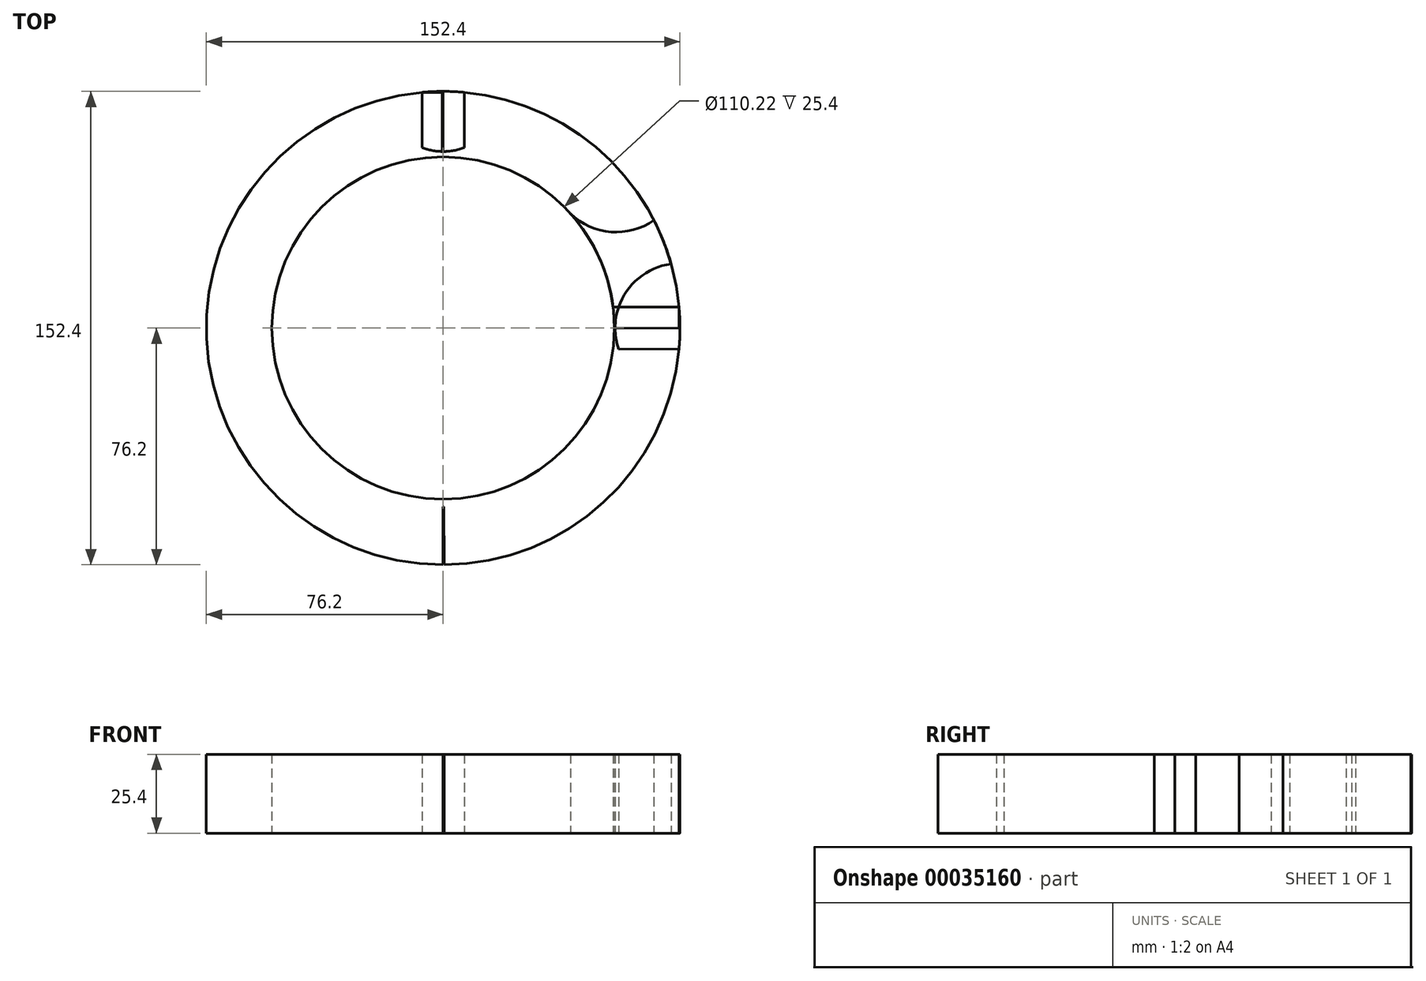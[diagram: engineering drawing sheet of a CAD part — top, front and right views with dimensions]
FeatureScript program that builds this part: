
annotation { "Feature Type Name" : "Feature", "Feature Type Description" : "" }
export const myFeature = defineFeature(function(context is Context, id is Id, definition is map)
    precondition{}
    {
        {
            var Q0;
            Q0=qCreatedBy(makeId("Top.planeOp"),FACE);
            var sketch = newSketch(context, id + "F0", { "sketchPlane" : qUnion([Q0])});
            skCircle(sketch, "E0", {"center": v(0, 0) * mm, "radius": 76.2 * mm});
            skLineSegment(sketch, "E1.bottom", {"start": v(-6.77, 75.9) * mm, "end": v(0, 75.9) * mm});
            skLineSegment(sketch, "E1.top", {"start": v(-6.77, -76.2) * mm, "end": v(0, -76.2) * mm});
            skLineSegment(sketch, "E1.left", {"start": v(-6.77, 75.9) * mm, "end": v(-6.77, -76.2) * mm});
            skLineSegment(sketch, "E1.right", {"start": v(0, 75.9) * mm, "end": v(0, -76.2) * mm});
            skLineSegment(sketch, "E2.MirrorCS", {"start": v(6.77, 75.9) * mm, "end": v(6.77, -76.2) * mm});
            skLineSegment(sketch, "E3", {"start": v(75.9, 6.7) * mm, "end": v(0, 6.7) * mm});
            skLineSegment(sketch, "E4", {"start": v(75.9, 0) * mm, "end": v(0, -0.15) * mm});
            skLineSegment(sketch, "E5.MirrorCS", {"start": v(75.93, -6.7) * mm, "end": v(0.03, -7.01) * mm});
            skLineSegment(sketch, "E6.MirrorCS", {"start": v(0.3, -76.2) * mm, "end": v(-0.3, 75.9) * mm});
            skLineSegment(sketch, "E7.MirrorCS", {"start": v(-75.9, 6.7) * mm, "end": v(0, 6.7) * mm});
            skLineSegment(sketch, "E8.MirrorCS", {"start": v(-75.93, -6.7) * mm, "end": v(-0.03, -7.01) * mm});
            skLineSegment(sketch, "E9", {"start": v(-76.2, 0) * mm, "end": v(-0.03, -0.3) * mm});
            skCircle(sketch, "E10", {"center": v(0, 75.9) * mm, "radius": 19.05 * mm});
            skCircle(sketch, "E11", {"center": v(-55.68, 52.02) * mm, "radius": 21.13 * mm});
            skCircle(sketch, "E12.MirrorC", {"center": v(-56.1, -52.18) * mm, "radius": 21.13 * mm});
            skCircle(sketch, "E13.MirrorC", {"center": v(-0.6, -76.5) * mm, "radius": 19.05 * mm});
            skCircle(sketch, "E14.MirrorC", {"center": v(56.1, -52.18) * mm, "radius": 21.13 * mm});
            skCircle(sketch, "E15.MirrorC", {"center": v(55.68, 52.02) * mm, "radius": 21.13 * mm});
            skCircle(sketch, "E16", {"center": v(-76.2, 0) * mm, "radius": 20.86 * mm});
            skCircle(sketch, "E17.MirrorC", {"center": v(76.2, 0) * mm, "radius": 20.86 * mm});
            skCircle(sketch, "E18", {"center": v(0, 0) * mm, "radius": 55.1 * mm});
            skLineSegment(sketch, "E19.bottom", {"start": v(75.9, 0) * mm, "end": v(97.82, 0) * mm});
            skLineSegment(sketch, "E19.top", {"start": v(75.9, 21.09) * mm, "end": v(97.82, 21.09) * mm});
            skLineSegment(sketch, "E19.left", {"start": v(75.9, 0) * mm, "end": v(75.9, 21.09) * mm});
            skLineSegment(sketch, "E19.right", {"start": v(97.82, 0) * mm, "end": v(97.82, 21.09) * mm});
            skLineSegment(sketch, "E20.bottom", {"start": v(55.68, 52.02) * mm, "end": v(75.71, 52.02) * mm});
            skLineSegment(sketch, "E20.top", {"start": v(55.68, 73.25) * mm, "end": v(75.71, 73.25) * mm});
            skLineSegment(sketch, "E20.left", {"start": v(55.68, 52.02) * mm, "end": v(55.68, 73.25) * mm});
            skLineSegment(sketch, "E20.right", {"start": v(75.71, 52.02) * mm, "end": v(75.71, 73.25) * mm});
            skLineSegment(sketch, "E21.bottom", {"start": v(-0.3, 75.9) * mm, "end": v(-19.7, 75.9) * mm});
            skLineSegment(sketch, "E21.top", {"start": v(-0.3, 95.36) * mm, "end": v(-19.7, 95.36) * mm});
            skLineSegment(sketch, "E21.left", {"start": v(-0.3, 75.9) * mm, "end": v(-0.3, 95.36) * mm});
            skLineSegment(sketch, "E21.right", {"start": v(-19.7, 75.9) * mm, "end": v(-19.7, 95.36) * mm});
            skLineSegment(sketch, "E22.bottom", {"start": v(-55.68, 52.02) * mm, "end": v(-76.2, 52.02) * mm});
            skLineSegment(sketch, "E22.top", {"start": v(-55.68, 74.45) * mm, "end": v(-76.2, 74.45) * mm});
            skLineSegment(sketch, "E22.left", {"start": v(-55.68, 52.02) * mm, "end": v(-55.68, 74.45) * mm});
            skLineSegment(sketch, "E22.right", {"start": v(-76.2, 52.02) * mm, "end": v(-76.2, 74.45) * mm});
            skLineSegment(sketch, "E23.bottom", {"start": v(-76.2, 0) * mm, "end": v(-97.1, 0) * mm});
            skLineSegment(sketch, "E23.top", {"start": v(-76.2, 20.85) * mm, "end": v(-97.1, 20.85) * mm});
            skLineSegment(sketch, "E23.left", {"start": v(-76.2, 0) * mm, "end": v(-76.2, 20.85) * mm});
            skLineSegment(sketch, "E23.right", {"start": v(-97.1, 0) * mm, "end": v(-97.1, 20.85) * mm});
            skLineSegment(sketch, "E24.bottom", {"start": v(-56.1, -52.18) * mm, "end": v(-76.67, -52.18) * mm});
            skLineSegment(sketch, "E24.top", {"start": v(-56.1, -74.09) * mm, "end": v(-76.67, -74.09) * mm});
            skLineSegment(sketch, "E24.left", {"start": v(-56.1, -52.18) * mm, "end": v(-56.1, -74.09) * mm});
            skLineSegment(sketch, "E24.right", {"start": v(-76.67, -52.18) * mm, "end": v(-76.67, -74.09) * mm});
            skLineSegment(sketch, "E25.bottom", {"start": v(0.3, -76.5) * mm, "end": v(-19.23, -76.5) * mm});
            skLineSegment(sketch, "E25.top", {"start": v(0.3, -96.2) * mm, "end": v(-19.23, -96.2) * mm});
            skLineSegment(sketch, "E25.left", {"start": v(0.3, -76.5) * mm, "end": v(0.3, -96.2) * mm});
            skLineSegment(sketch, "E25.right", {"start": v(-19.23, -76.5) * mm, "end": v(-19.23, -96.2) * mm});
            skLineSegment(sketch, "E26.bottom", {"start": v(56.1, -52.18) * mm, "end": v(76.2, -52.18) * mm});
            skLineSegment(sketch, "E26.top", {"start": v(56.1, -73.85) * mm, "end": v(76.2, -73.85) * mm});
            skLineSegment(sketch, "E26.left", {"start": v(56.1, -52.18) * mm, "end": v(56.1, -73.85) * mm});
            skLineSegment(sketch, "E26.right", {"start": v(76.2, -52.18) * mm, "end": v(76.2, -73.85) * mm});
            skSolve(sketch);
        }
        {
            var Q0;
            {var subQ3=sQuery(id+"F0.wireOp",EDGE,"E8.MirrorCS");var subQ5=sQuery(id+"F0.wireOp",EDGE,"E16");var subQ7=makeQuery(id+"F0.imprint","INTERSECT",VERTEX,{"derivedFrom":[subQ3,subQ5]});Q0=makeQuery(id+"F0.imprint","IMPRINT",FACE,{"disambiguationData":[TD([[makeQuery(id+"F0.imprint","IMPRINT",EDGE,{"disambiguationData":[TD([[subQ7,-1.0]])],"derivedFrom":subQ3}),1.0]])]});}
            var Q1;
            {var subQ0=sQuery(id+"F0.wireOp",EDGE,"E14.MirrorC");var subQ1=sQuery(id+"F0.wireOp",EDGE,"E0");var subQ3=makeQuery(id+"F0.imprint","INTERSECT",VERTEX,{"disambiguationData":[OD(0.0)],"derivedFrom":[subQ1,subQ0]});Q1=makeQuery(id+"F0.imprint","IMPRINT",FACE,{"disambiguationData":[TD([[makeQuery(id+"F0.imprint","IMPRINT",EDGE,{"disambiguationData":[TD([[subQ3,-1.0]])],"derivedFrom":subQ1}),1.0]])]});}
            var Q2;
            {var subQ3=sQuery(id+"F0.wireOp",EDGE,"E0");var subQ5=sQuery(id+"F0.wireOp",EDGE,"E7.MirrorCS");var subQ7=makeQuery(id+"F0.imprint","INTERSECT",VERTEX,{"derivedFrom":[subQ3,subQ5]});Q2=makeQuery(id+"F0.imprint","IMPRINT",FACE,{"disambiguationData":[TD([[makeQuery(id+"F0.imprint","IMPRINT",EDGE,{"disambiguationData":[TD([[subQ7,-1.0]])],"derivedFrom":subQ3}),1.0]])]});}
            var Q3;
            {var subQ3=sQuery(id+"F0.wireOp",EDGE,"E1.right");var subQ5=sQuery(id+"F0.wireOp",EDGE,"E10");var subQ6=makeQuery(id+"F0.imprint","INTERSECT",VERTEX,{"derivedFrom":[subQ3,subQ5]});Q3=makeQuery(id+"F0.imprint","IMPRINT",FACE,{"disambiguationData":[TD([[makeQuery(id+"F0.imprint","IMPRINT",EDGE,{"disambiguationData":[TD([[subQ6,-1.0]])],"derivedFrom":subQ3}),-1.0]])]});}
            var Q4;
            {var subQ6=sQuery(id+"F0.wireOp",EDGE,"E1.bottom");Q4=makeQuery(id+"F0.imprint","IMPRINT",FACE,{"disambiguationData":[TD([[makeQuery(id+"F0.imprint","IMPRINT",EDGE,{"derivedFrom":subQ6}),-1.0]])]});}
            var Q5;
            {var subQ1=sQuery(id+"F0.wireOp",EDGE,"E2.MirrorCS");var subQ3=sQuery(id+"F0.wireOp",EDGE,"E0");var subQ5=makeQuery(id+"F0.imprint","INTERSECT",VERTEX,{"disambiguationData":[OD(1.0)],"derivedFrom":[subQ3,subQ1]});Q5=makeQuery(id+"F0.imprint","IMPRINT",FACE,{"disambiguationData":[TD([[makeQuery(id+"F0.imprint","IMPRINT",EDGE,{"disambiguationData":[TD([[subQ5,-1.0]])],"derivedFrom":subQ3}),1.0]])]});}
            var Q6;
            {var subQ1=sQuery(id+"F0.wireOp",EDGE,"E7.MirrorCS");var subQ3=sQuery(id+"F0.wireOp",EDGE,"E0");var subQ5=makeQuery(id+"F0.imprint","INTERSECT",VERTEX,{"derivedFrom":[subQ3,subQ1]});Q6=makeQuery(id+"F0.imprint","IMPRINT",FACE,{"disambiguationData":[TD([[makeQuery(id+"F0.imprint","IMPRINT",EDGE,{"disambiguationData":[TD([[subQ5,1.0]])],"derivedFrom":subQ3}),1.0]])]});}
            var Q7;
            {var subQ0=sQuery(id+"F0.wireOp",EDGE,"E0");var subQ3=sQuery(id+"F0.wireOp",EDGE,"E17.MirrorC");var subQ4=makeQuery(id+"F0.imprint","INTERSECT",VERTEX,{"disambiguationData":[OD(0.0)],"derivedFrom":[subQ0,subQ3]});Q7=makeQuery(id+"F0.imprint","IMPRINT",FACE,{"disambiguationData":[TD([[makeQuery(id+"F0.imprint","IMPRINT",EDGE,{"disambiguationData":[TD([[subQ4,-1.0]])],"derivedFrom":subQ0}),1.0]])]});}
            var Q8;
            {var subQ1=sQuery(id+"F0.wireOp",EDGE,"E3");var subQ3=sQuery(id+"F0.wireOp",EDGE,"E0");var subQ5=makeQuery(id+"F0.imprint","INTERSECT",VERTEX,{"derivedFrom":[subQ3,subQ1]});Q8=makeQuery(id+"F0.imprint","IMPRINT",FACE,{"disambiguationData":[TD([[makeQuery(id+"F0.imprint","IMPRINT",EDGE,{"disambiguationData":[TD([[subQ5,-1.0]])],"derivedFrom":subQ3}),1.0]])]});}
            var Q9;
            {var subQ1=sQuery(id+"F0.wireOp",EDGE,"E11");var subQ5=sQuery(id+"F0.wireOp",EDGE,"E0");var subQ8=makeQuery(id+"F0.imprint","INTERSECT",VERTEX,{"disambiguationData":[OD(1.0)],"derivedFrom":[subQ5,subQ1]});Q9=makeQuery(id+"F0.imprint","IMPRINT",FACE,{"disambiguationData":[TD([[makeQuery(id+"F0.imprint","IMPRINT",EDGE,{"disambiguationData":[TD([[subQ8,-1.0]])],"derivedFrom":subQ5}),1.0]])]});}
            var Q10;
            {var subQ0=sQuery(id+"F0.wireOp",EDGE,"E0");var subQ3=sQuery(id+"F0.wireOp",EDGE,"E3");var subQ4=makeQuery(id+"F0.imprint","INTERSECT",VERTEX,{"derivedFrom":[subQ0,subQ3]});Q10=makeQuery(id+"F0.imprint","IMPRINT",FACE,{"disambiguationData":[TD([[makeQuery(id+"F0.imprint","IMPRINT",EDGE,{"disambiguationData":[TD([[subQ4,1.0]])],"derivedFrom":subQ0}),1.0]])]});}
            var Q11;
            {var subQ0=sQuery(id+"F0.wireOp",EDGE,"E0");var subQ3=sQuery(id+"F0.wireOp",EDGE,"E10");var subQ4=makeQuery(id+"F0.imprint","INTERSECT",VERTEX,{"disambiguationData":[OD(1.0)],"derivedFrom":[subQ0,subQ3]});Q11=makeQuery(id+"F0.imprint","IMPRINT",FACE,{"disambiguationData":[TD([[makeQuery(id+"F0.imprint","IMPRINT",EDGE,{"disambiguationData":[TD([[subQ4,-1.0]])],"derivedFrom":subQ0}),1.0]])]});}
            var Q12;
            {var subQ1=sQuery(id+"F0.wireOp",EDGE,"E9");var subQ5=sQuery(id+"F0.wireOp",EDGE,"E0");var subQ6=makeQuery(id+"F0.imprint","INTERSECT",VERTEX,{"derivedFrom":[subQ5,subQ1]});Q12=makeQuery(id+"F0.imprint","IMPRINT",FACE,{"disambiguationData":[TD([[makeQuery(id+"F0.imprint","IMPRINT",EDGE,{"disambiguationData":[TD([[subQ6,-1.0]])],"derivedFrom":subQ5}),1.0]])]});}
            var Q13;
            {var subQ6=sQuery(id+"F0.wireOp",EDGE,"E0");var subQ12=sQuery(id+"F0.wireOp",EDGE,"E16");var subQ13=makeQuery(id+"F0.imprint","INTERSECT",VERTEX,{"disambiguationData":[OD(1.0)],"derivedFrom":[subQ6,subQ12]});Q13=makeQuery(id+"F0.imprint","IMPRINT",FACE,{"disambiguationData":[TD([[makeQuery(id+"F0.imprint","IMPRINT",EDGE,{"disambiguationData":[TD([[subQ13,-1.0]])],"derivedFrom":subQ6}),1.0]])]});}
            var Q14;
            {var subQ3=sQuery(id+"F0.wireOp",EDGE,"E1.left");var subQ5=sQuery(id+"F0.wireOp",EDGE,"E10");var subQ6=makeQuery(id+"F0.imprint","INTERSECT",VERTEX,{"derivedFrom":[subQ3,subQ5]});Q14=makeQuery(id+"F0.imprint","IMPRINT",FACE,{"disambiguationData":[TD([[makeQuery(id+"F0.imprint","IMPRINT",EDGE,{"disambiguationData":[TD([[subQ6,-1.0]])],"derivedFrom":subQ3}),1.0]])]});}
            var Q15;
            {var subQ3=sQuery(id+"F0.wireOp",EDGE,"E4");var subQ5=sQuery(id+"F0.wireOp",EDGE,"E17.MirrorC");var subQ7=makeQuery(id+"F0.imprint","INTERSECT",VERTEX,{"derivedFrom":[subQ3,subQ5]});Q15=makeQuery(id+"F0.imprint","IMPRINT",FACE,{"disambiguationData":[TD([[makeQuery(id+"F0.imprint","IMPRINT",EDGE,{"disambiguationData":[TD([[subQ7,-1.0]])],"derivedFrom":subQ3}),1.0]])]});}
            var Q16;
            {var subQ3=sQuery(id+"F0.wireOp",EDGE,"E3");var subQ5=sQuery(id+"F0.wireOp",EDGE,"E17.MirrorC");var subQ7=makeQuery(id+"F0.imprint","INTERSECT",VERTEX,{"derivedFrom":[subQ3,subQ5]});Q16=makeQuery(id+"F0.imprint","IMPRINT",FACE,{"disambiguationData":[TD([[makeQuery(id+"F0.imprint","IMPRINT",EDGE,{"disambiguationData":[TD([[subQ7,-1.0]])],"derivedFrom":subQ3}),1.0]])]});}
            var Q17;
            {var subQ3=sQuery(id+"F0.wireOp",EDGE,"E1.left");var subQ5=sQuery(id+"F0.wireOp",EDGE,"E0");var subQ7=makeQuery(id+"F0.imprint","INTERSECT",VERTEX,{"derivedFrom":[subQ5,subQ3]});Q17=makeQuery(id+"F0.imprint","IMPRINT",FACE,{"disambiguationData":[TD([[makeQuery(id+"F0.imprint","IMPRINT",EDGE,{"disambiguationData":[TD([[subQ7,1.0]])],"derivedFrom":subQ3}),1.0]])]});}
            var Q18;
            {var subQ0=sQuery(id+"F0.wireOp",EDGE,"E12.MirrorC");var subQ1=sQuery(id+"F0.wireOp",EDGE,"E0");var subQ3=makeQuery(id+"F0.imprint","INTERSECT",VERTEX,{"disambiguationData":[OD(0.0)],"derivedFrom":[subQ1,subQ0]});Q18=makeQuery(id+"F0.imprint","IMPRINT",FACE,{"disambiguationData":[TD([[makeQuery(id+"F0.imprint","IMPRINT",EDGE,{"disambiguationData":[TD([[subQ3,-1.0]])],"derivedFrom":subQ1}),1.0]])]});}
            var Q19;
            {var subQ0=sQuery(id+"F0.wireOp",EDGE,"E18");var subQ3=sQuery(id+"F0.wireOp",EDGE,"E1.right");var subQ4=makeQuery(id+"F0.imprint","INTERSECT",VERTEX,{"disambiguationData":[OD(1.0)],"derivedFrom":[subQ3,subQ0]});Q19=makeQuery(id+"F0.imprint","IMPRINT",FACE,{"disambiguationData":[TD([[makeQuery(id+"F0.imprint","IMPRINT",EDGE,{"disambiguationData":[TD([[subQ4,-1.0]])],"derivedFrom":subQ3}),1.0]])]});}
            var Q20;
            {var subQ3=sQuery(id+"F0.wireOp",EDGE,"E0");var subQ8=sQuery(id+"F0.wireOp",EDGE,"E13.MirrorC");var subQ11=makeQuery(id+"F0.imprint","INTERSECT",VERTEX,{"disambiguationData":[OD(1.0)],"derivedFrom":[subQ3,subQ8]});Q20=makeQuery(id+"F0.imprint","IMPRINT",FACE,{"disambiguationData":[TD([[makeQuery(id+"F0.imprint","IMPRINT",EDGE,{"disambiguationData":[TD([[subQ11,-1.0]])],"derivedFrom":subQ3}),1.0]])]});}
            var Q21;
            {var subQ7=sQuery(id+"F0.wireOp",EDGE,"E1.bottom");Q21=makeQuery(id+"F0.imprint","IMPRINT",FACE,{"disambiguationData":[TD([[makeQuery(id+"F0.imprint","IMPRINT",EDGE,{"derivedFrom":subQ7}),1.0]])]});}
            var Q22;
            {var subQ3=sQuery(id+"F0.wireOp",EDGE,"E7.MirrorCS");var subQ5=sQuery(id+"F0.wireOp",EDGE,"E16");var subQ7=makeQuery(id+"F0.imprint","INTERSECT",VERTEX,{"derivedFrom":[subQ3,subQ5]});Q22=makeQuery(id+"F0.imprint","IMPRINT",FACE,{"disambiguationData":[TD([[makeQuery(id+"F0.imprint","IMPRINT",EDGE,{"disambiguationData":[TD([[subQ7,-1.0]])],"derivedFrom":subQ3}),-1.0]])]});}
            var Q23;
            {var subQ1=sQuery(id+"F0.wireOp",EDGE,"E8.MirrorCS");var subQ3=sQuery(id+"F0.wireOp",EDGE,"E0");var subQ5=makeQuery(id+"F0.imprint","INTERSECT",VERTEX,{"derivedFrom":[subQ3,subQ1]});Q23=makeQuery(id+"F0.imprint","IMPRINT",FACE,{"disambiguationData":[TD([[makeQuery(id+"F0.imprint","IMPRINT",EDGE,{"disambiguationData":[TD([[subQ5,-1.0]])],"derivedFrom":subQ3}),1.0]])]});}
            var Q24;
            {var subQ1=sQuery(id+"F0.wireOp",EDGE,"E2.MirrorCS");var subQ3=sQuery(id+"F0.wireOp",EDGE,"E0");var subQ5=makeQuery(id+"F0.imprint","INTERSECT",VERTEX,{"disambiguationData":[OD(0.0)],"derivedFrom":[subQ3,subQ1]});Q24=makeQuery(id+"F0.imprint","IMPRINT",FACE,{"disambiguationData":[TD([[makeQuery(id+"F0.imprint","IMPRINT",EDGE,{"disambiguationData":[TD([[subQ5,1.0]])],"derivedFrom":subQ3}),1.0]])]});}
            var Q25;
            {var subQ1=sQuery(id+"F0.wireOp",EDGE,"E11");var subQ4=sQuery(id+"F0.wireOp",EDGE,"E0");var subQ5=makeQuery(id+"F0.imprint","INTERSECT",VERTEX,{"disambiguationData":[OD(0.0)],"derivedFrom":[subQ4,subQ1]});Q25=makeQuery(id+"F0.imprint","IMPRINT",FACE,{"disambiguationData":[TD([[makeQuery(id+"F0.imprint","IMPRINT",EDGE,{"disambiguationData":[TD([[subQ5,-1.0]])],"derivedFrom":subQ4}),1.0]])]});}
            var Q26;
            {var subQ0=sQuery(id+"F0.wireOp",EDGE,"E15.MirrorC");var subQ3=sQuery(id+"F0.wireOp",EDGE,"E0");var subQ6=makeQuery(id+"F0.imprint","INTERSECT",VERTEX,{"disambiguationData":[OD(0.0)],"derivedFrom":[subQ3,subQ0]});Q26=makeQuery(id+"F0.imprint","IMPRINT",FACE,{"disambiguationData":[TD([[makeQuery(id+"F0.imprint","IMPRINT",EDGE,{"disambiguationData":[TD([[subQ6,-1.0]])],"derivedFrom":subQ3}),1.0]])]});}
            var Q27;
            {var subQ0=sQuery(id+"F0.wireOp",EDGE,"E18");var subQ3=sQuery(id+"F0.wireOp",EDGE,"E1.left");var subQ4=makeQuery(id+"F0.imprint","INTERSECT",VERTEX,{"disambiguationData":[OD(1.0)],"derivedFrom":[subQ3,subQ0]});Q27=makeQuery(id+"F0.imprint","IMPRINT",FACE,{"disambiguationData":[TD([[makeQuery(id+"F0.imprint","IMPRINT",EDGE,{"disambiguationData":[TD([[subQ4,-1.0]])],"derivedFrom":subQ3}),1.0]])]});}
            var Q28;
            {var subQ1=sQuery(id+"F0.wireOp",EDGE,"E6.MirrorCS");var subQ5=sQuery(id+"F0.wireOp",EDGE,"E0");var subQ6=makeQuery(id+"F0.imprint","INTERSECT",VERTEX,{"derivedFrom":[subQ5,subQ1]});Q28=makeQuery(id+"F0.imprint","IMPRINT",FACE,{"disambiguationData":[TD([[makeQuery(id+"F0.imprint","IMPRINT",EDGE,{"disambiguationData":[TD([[subQ6,-1.0]])],"derivedFrom":subQ5}),1.0]])]});}
            var Q29;
            {var subQ0=sQuery(id+"F0.wireOp",EDGE,"E13.MirrorC");var subQ3=sQuery(id+"F0.wireOp",EDGE,"E0");var subQ4=makeQuery(id+"F0.imprint","INTERSECT",VERTEX,{"disambiguationData":[OD(0.0)],"derivedFrom":[subQ3,subQ0]});Q29=makeQuery(id+"F0.imprint","IMPRINT",FACE,{"disambiguationData":[TD([[makeQuery(id+"F0.imprint","IMPRINT",EDGE,{"disambiguationData":[TD([[subQ4,-1.0]])],"derivedFrom":subQ3}),1.0]])]});}
            var Q30;
            {var subQ3=sQuery(id+"F0.wireOp",EDGE,"E1.right");var subQ5=sQuery(id+"F0.wireOp",EDGE,"E10");var subQ7=makeQuery(id+"F0.imprint","INTERSECT",VERTEX,{"derivedFrom":[subQ3,subQ5]});Q30=makeQuery(id+"F0.imprint","IMPRINT",FACE,{"disambiguationData":[TD([[makeQuery(id+"F0.imprint","IMPRINT",EDGE,{"disambiguationData":[TD([[subQ7,-1.0]])],"derivedFrom":subQ3}),1.0]])]});}
            var Q31;
            {var subQ1=sQuery(id+"F0.wireOp",EDGE,"E15.MirrorC");var subQ5=sQuery(id+"F0.wireOp",EDGE,"E0");var subQ8=makeQuery(id+"F0.imprint","INTERSECT",VERTEX,{"disambiguationData":[OD(1.0)],"derivedFrom":[subQ5,subQ1]});Q31=makeQuery(id+"F0.imprint","IMPRINT",FACE,{"disambiguationData":[TD([[makeQuery(id+"F0.imprint","IMPRINT",EDGE,{"disambiguationData":[TD([[subQ8,-1.0]])],"derivedFrom":subQ5}),1.0]])]});}
            var Q32;
            {var subQ0=sQuery(id+"F0.wireOp",EDGE,"E17.MirrorC");var subQ3=sQuery(id+"F0.wireOp",EDGE,"E0");var subQ4=makeQuery(id+"F0.imprint","INTERSECT",VERTEX,{"disambiguationData":[OD(1.0)],"derivedFrom":[subQ3,subQ0]});Q32=makeQuery(id+"F0.imprint","IMPRINT",FACE,{"disambiguationData":[TD([[makeQuery(id+"F0.imprint","IMPRINT",EDGE,{"disambiguationData":[TD([[subQ4,-1.0]])],"derivedFrom":subQ3}),1.0]])]});}
            var Q33;
            {var subQ0=sQuery(id+"F0.wireOp",EDGE,"E18");var subQ3=sQuery(id+"F0.wireOp",EDGE,"E2.MirrorCS");var subQ4=makeQuery(id+"F0.imprint","INTERSECT",VERTEX,{"disambiguationData":[OD(1.0)],"derivedFrom":[subQ3,subQ0]});Q33=makeQuery(id+"F0.imprint","IMPRINT",FACE,{"disambiguationData":[TD([[makeQuery(id+"F0.imprint","IMPRINT",EDGE,{"disambiguationData":[TD([[subQ4,-1.0]])],"derivedFrom":subQ3}),-1.0]])]});}
            var Q34;
            {var subQ1=sQuery(id+"F0.wireOp",EDGE,"E10");var subQ3=sQuery(id+"F0.wireOp",EDGE,"E0");var subQ5=makeQuery(id+"F0.imprint","INTERSECT",VERTEX,{"disambiguationData":[OD(1.0)],"derivedFrom":[subQ3,subQ1]});Q34=makeQuery(id+"F0.imprint","IMPRINT",FACE,{"disambiguationData":[TD([[makeQuery(id+"F0.imprint","IMPRINT",EDGE,{"disambiguationData":[TD([[subQ5,-1.0]])],"derivedFrom":subQ1}),1.0]])]});}
            extrude(context, id + "F1", {"entities" : qUnion([Q0, Q1, Q2, Q3, Q4, Q5, Q6, Q7, Q8, Q9, Q10, Q11, Q12, Q13, Q14, Q15, Q16, Q17, Q18, Q19, Q20, Q21, Q22, Q23, Q24, Q25, Q26, Q27, Q28, Q29, Q30, Q31, Q32, Q33, Q34]), "depth" : 25.4 * mm});
        }
        {
            var Q0;
            {var subQ3=sQuery(id+"F0.wireOp",EDGE,"E1.left");var subQ5=sQuery(id+"F0.wireOp",EDGE,"E18");var subQ7=makeQuery(id+"F0.imprint","INTERSECT",VERTEX,{"disambiguationData":[OD(0.0)],"derivedFrom":[subQ3,subQ5]});Q0=makeQuery(id+"F0.imprint","IMPRINT",FACE,{"disambiguationData":[TD([[makeQuery(id+"F0.imprint","IMPRINT",EDGE,{"disambiguationData":[TD([[subQ7,-1.0]])],"derivedFrom":subQ3}),1.0]])]});}
            var Q1;
            {var subQ3=sQuery(id+"F0.wireOp",EDGE,"E3");var subQ5=sQuery(id+"F0.wireOp",EDGE,"E2.MirrorCS");var subQ7=makeQuery(id+"F0.imprint","INTERSECT",VERTEX,{"derivedFrom":[subQ5,subQ3]});Q1=makeQuery(id+"F0.imprint","IMPRINT",FACE,{"disambiguationData":[TD([[makeQuery(id+"F0.imprint","IMPRINT",EDGE,{"disambiguationData":[TD([[subQ7,-1.0]])],"derivedFrom":subQ5}),1.0]])]});}
            var Q2;
            {var subQ1=sQuery(id+"F0.wireOp",EDGE,"E9");var subQ5=sQuery(id+"F0.wireOp",EDGE,"E1.left");var subQ6=makeQuery(id+"F0.imprint","INTERSECT",VERTEX,{"derivedFrom":[subQ5,subQ1]});Q2=makeQuery(id+"F0.imprint","IMPRINT",FACE,{"disambiguationData":[TD([[makeQuery(id+"F0.imprint","IMPRINT",EDGE,{"disambiguationData":[TD([[subQ6,-1.0]])],"derivedFrom":subQ5}),-1.0]])]});}
            var Q3;
            {var subQ3=sQuery(id+"F0.wireOp",EDGE,"E2.MirrorCS");var subQ5=sQuery(id+"F0.wireOp",EDGE,"E5.MirrorCS");var subQ6=makeQuery(id+"F0.imprint","INTERSECT",VERTEX,{"derivedFrom":[subQ3,subQ5]});Q3=makeQuery(id+"F0.imprint","IMPRINT",FACE,{"disambiguationData":[TD([[makeQuery(id+"F0.imprint","IMPRINT",EDGE,{"disambiguationData":[TD([[subQ6,-1.0]])],"derivedFrom":subQ3}),-1.0]])]});}
            extrude(context, id + "F2", {"entities" : qUnion([Q0, Q1, Q2, Q3]), "operationType" : NewBodyOperationType.REMOVE, "depth" : 25.4 * mm});
        }
        {
            var Q0;
            {var subQ1=sQuery(id+"F0.wireOp",EDGE,"E0");var subQ5=sQuery(id+"F0.wireOp",EDGE,"E5.MirrorCS");var subQ6=makeQuery(id+"F0.imprint","INTERSECT",VERTEX,{"derivedFrom":[subQ1,subQ5]});Q0=makeQuery(id+"F0.imprint","IMPRINT",FACE,{"disambiguationData":[TD([[makeQuery(id+"F0.imprint","IMPRINT",EDGE,{"disambiguationData":[TD([[subQ6,-1.0]])],"derivedFrom":subQ1}),1.0]])]});}
            var Q1;
            {var subQ0=sQuery(id+"F0.wireOp",EDGE,"E17.MirrorC");var subQ3=sQuery(id+"F0.wireOp",EDGE,"E3");var subQ4=makeQuery(id+"F0.imprint","INTERSECT",VERTEX,{"derivedFrom":[subQ3,subQ0]});Q1=makeQuery(id+"F0.imprint","IMPRINT",FACE,{"disambiguationData":[TD([[makeQuery(id+"F0.imprint","IMPRINT",EDGE,{"disambiguationData":[TD([[subQ4,1.0]])],"derivedFrom":subQ0}),-1.0]])]});}
            var Q2;
            {var subQ3=sQuery(id+"F0.wireOp",EDGE,"E0");var subQ6=sQuery(id+"F0.wireOp",EDGE,"E2.MirrorCS");var subQ10=makeQuery(id+"F0.imprint","INTERSECT",VERTEX,{"disambiguationData":[OD(0.0)],"derivedFrom":[subQ3,subQ6]});Q2=makeQuery(id+"F0.imprint","IMPRINT",FACE,{"disambiguationData":[TD([[makeQuery(id+"F0.imprint","IMPRINT",EDGE,{"disambiguationData":[TD([[subQ10,-1.0]])],"derivedFrom":subQ3}),1.0]])]});}
            var Q3;
            {var subQ0=sQuery(id+"F0.wireOp",EDGE,"E21.bottom");var subQ1=sQuery(id+"F0.wireOp",EDGE,"E1.left");var subQ2=makeQuery(id+"F0.imprint","INTERSECT",VERTEX,{"derivedFrom":[subQ1,subQ0]});Q3=makeQuery(id+"F0.imprint","IMPRINT",FACE,{"disambiguationData":[TD([[makeQuery(id+"F0.imprint","IMPRINT",EDGE,{"disambiguationData":[TD([[subQ2,-1.0]])],"derivedFrom":subQ1}),1.0]])]});}
            extrude(context, id + "F3", {"entities" : qUnion([Q0, Q1, Q2, Q3]), "depth" : 25.4 * mm});
        }
        {
            var Q0;
            Q0=makeQuery(id+"F3.opExtrude","SWEPT_BODY",BODY,{"disambiguationData":[OSD([sQuery(id+"F0.wireOp",EDGE,"E0"),sQuery(id+"F0.wireOp",EDGE,"E3"),sQuery(id+"F0.wireOp",EDGE,"E5.MirrorCS"),sQuery(id+"F0.wireOp",EDGE,"E17.MirrorC"),sQuery(id+"F0.wireOp",EDGE,"E19.bottom"),sQuery(id+"F0.wireOp",EDGE,"E19.left")])]});
            var Q1;
            Q1=makeQuery(id+"F3.opExtrude","SWEPT_BODY",BODY,{"disambiguationData":[OSD([sQuery(id+"F0.wireOp",EDGE,"E0"),sQuery(id+"F0.wireOp",EDGE,"E1.bottom"),sQuery(id+"F0.wireOp",EDGE,"E1.right"),sQuery(id+"F0.wireOp",EDGE,"E2.MirrorCS"),sQuery(id+"F0.wireOp",EDGE,"E10"),sQuery(id+"F0.wireOp",EDGE,"E21.left")])]});
            var Q2;
            Q2=makeQuery(id+"F3.opExtrude","SWEPT_BODY",BODY,{"disambiguationData":[OSD([sQuery(id+"F0.wireOp",EDGE,"E1.left"),sQuery(id+"F0.wireOp",EDGE,"E6.MirrorCS"),sQuery(id+"F0.wireOp",EDGE,"E10"),sQuery(id+"F0.wireOp",EDGE,"E21.bottom")])]});
            booleanBodies(context, id + "F4", {"operationType" : BooleanOperationType.UNION, "tools" : qUnion([Q0, Q1, Q2])});
        }
    });
